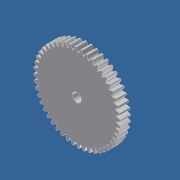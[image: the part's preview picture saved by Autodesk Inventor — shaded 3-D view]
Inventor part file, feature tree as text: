
AUTODESK INVENTOR PART (.ipt)
format: ipt  version: unknown  size: 573,440 bytes
history: native  units: in
note: dims shown in document units (in); Inventor stores cm internally (conversion verified against a paired STEP export)
features: extrude x3, sketch x3, imported_body x1
ambient origin geometry x8: Origin, YZ Plane, XZ Plane, XY Plane, X Axis, Y Axis, Z Axis, Center Point
bodies: Solid1 (feature_tree)
feature tree (7):
  imported_body  "Base1"
  extrude  "Extrusion1"  Depth=0.63in TaperAngle=0.0deg
  extrude  "Extrusion2"  Depth=0.38in TaperAngle=0.0deg
  extrude  "Extrusion3"  Depth=0.171in
  sketch  "Sketch1"  dims[d0=0.215in d1=0.63in d2=0.0in]
  sketch  "Sketch2"  dims[d3=0.7in d6=0.38in d7=0.0in]
  sketch  "Sketch3"  dims[d8=0.15in d9=0.171in d10=0.3in d11=0.0in]
